# Revit family: Door_SS_The Sliding Door Company_4-Panel Quad Track
name_source: partatom
category: Doors
units: mm (PartAtom-declared; Revit-internal decimal feet)

## family parameters
Always vertical = Yes
Cut with Voids When Loaded = No
Host = Wall
OmniClass Number = 23.30.10.00
OmniClass Title = Doors
Room Calculation Point = No
Shared = No

## types (1)
- SS Room Divider - 4 Panel 4 Track - ABCD/DCBA
    2 1/2" Frame (No Support Dividers) = Max. H=108 in., Max. W=280 in. (72 in. panel width)
    Analytic Construction = <None>
    Clear Opening Height = 104 1/2"
    Configuration = ABCD/DCBA Configuration
    Construction Type = Top Mounted, Suspended System
    Description = 4 Panel Suspended System with 4 Track
    Finished Opening Height = 108"
    Finished Opening Width = 280"
    Function = Interior
    Glass Thickness = Available in: 5mm Tempered, 7mm,10mm,11mm Laminated Glass
    Height = 108"
    Limitations = Panel Width x System Height cannot exceed 7,400 square inches
    Manufacturer = The Sliding Door Company
    Model = Suspended System - Full Height System
    Panel Height = 105 3/4"
    Panel Width = 71 7/8"
    Rough Height = 108 5/8"
    Rough Width = 281 1/4"
    Stile and Rail = 2 1/2"
    Structural Support = Suspended Systems MUST be installed into structural wood header
    Thickness = 1 1/4"
    URL = https://www.slidingdoorco.com
    Wall Closure = By host
    Width = 280"

## geometry (parser evidence)
native form markers: Blend x3, Sweep x4
no freeform markers — native parametric forms only
